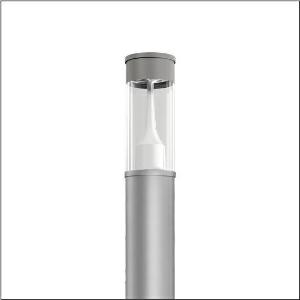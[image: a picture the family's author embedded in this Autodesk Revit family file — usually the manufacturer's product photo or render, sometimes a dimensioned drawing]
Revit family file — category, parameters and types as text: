
# Revit family: city-light_260_iq___pl1_2s_5xa5295jf14h_6623
name_source: partatom
category: Lighting Fixtures
units: mm (PartAtom-declared; Revit-internal decimal feet)

## family parameters
Cut with Voids When Loaded = No
Host = Face
Light Source = No
Part Type = Normal
Room Calculation Point = No
Round Connector Dimension = Use Diameter
Shared = No

## types (1)
- --- (1 x LED, 4740 lm, 19.3 W, 3000K)
    Apparent Load = 19 VA
    CIE Flux Codes = 23 62 94 96 100
    Color Rendering = 70
    Color Temperature = 3000K
    Default Elevation = 1800 mm
    Description = City-Light 260 iQ, light pillar, Module 540 iQ-SR, primary light control with 3 zone facetted reflector, of plastic, silver coated, highly specular, structured, primary optical cover: cover, of PMMA, transparent, light distribution: PL1.2s, primary light characteristic: symmetric, LED, High Power LED, rated luminous flux: 2.970lm, luminous efficacy: 154lm/W, light colour: 730, colour temperature: 3000K, control gear: ECG iQ, control: Auto-Match, Temp-Guard, Lumen-Switch, Night-Set, Smart-Wire, Light-Fading, Desk-Remote (wireless, voltage-free reading and setting of iQ features in the workshop via application-optimized NFC function/RFID function), optimised constant luminous flux control (CLO 2.0), Street-Remote, presetting dimming logarithmic, with terminal, 6-pole, max. 2.5mm², mains connection: 230..240V, AC, 50/60Hz, start of lifetime: 19W, end of service life: 21W, reduction: 10W, luminaire housing, cylindrical, of extruded aluminium section, coated, Siteco® metallic grey (DB 702S), length: 2.600mm, diameter: 200mm, Module 540 iQ-SR, traffic white (RAL 9016), equipment: standard, protection rating (complete): IP65, insulation class (complete): insulation class II (safety insulation), certification: CE, ENEC, VDE, packaging unit: 1 piece

Light Distribution: PL1.2s
    Height = 500 mm
    Lamp = 1 x LED
    Lamp Light Flux = 4740 lm
    Lamp Power = 19.3 W
    Lamp count = 1
    Length = 200 mm  [stored 0.656168 ft]
    Luminous efficacy = 246 lm/W
    Manufacturer = Siteco
    ModVariant = No
    Model = 5XA5295JF14H
    Mounting Place = Floor
    Mounting Type = Freestanding
    Number of Poles = 1
    OnlyDefault = Yes
    Power Factor = 1
    Product Name = City-Light 260 iQ | PL1.2s
    Product group = light pillar
    ProductGroupID = 1303
    Protection Class = Protection class II
    Protection Degree = IP 65
    RLX_Detail_Level = 1
    RLX_Emergency_Light_Flux = 0 lm
    RLX_Emergency_Type = 0
    RLX_Emergency_Type_DB = No
    RlxData = <blob elided: 28701 chars, md5=49f90516>
    Socket = socket
    Standby Power = 0 W
    System Light Flux = 4740 lm
    System Power = 19 W
    Type Comments = factory setting: luminous flux: 100 % | dim-lin: 254 | 403 mA
    Type Image = l_1006920.jpg
    URL = http://relux.com
    VarID = @adj_076667
    Voltage = 0 V
    Weight = 0.00 kg
    Width = 0 mm  [stored 0 ft]

note: [stored X ft] marks values corroborated as IEEE doubles in the binary element streams (Revit-internal decimal feet)

## geometry (parser evidence)
native form markers: Blend x4, Sweep x10
no freeform markers — native parametric forms only
